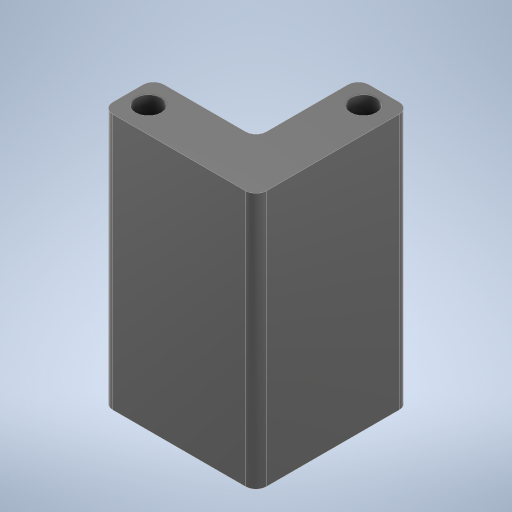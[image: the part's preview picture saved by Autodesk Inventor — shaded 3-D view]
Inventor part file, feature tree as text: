
AUTODESK INVENTOR PART (.ipt)
format: ipt  version: 2024 (Build 280153000, 153)  size: 234,496 bytes
history: native  units: in
note: dims shown in document units (in); Inventor stores cm internally (conversion verified against a paired STEP export)
features: fillet x2, sketch x2, extrude x1, hole x1
ambient origin geometry x8: Origin, YZ Plane, XZ Plane, XY Plane, X Axis, Y Axis, Z Axis, Center Point
bodies: Body1 (feature_tree)
feature tree (6):
  extrude  "Extrusion2"  Depth=1.1811in
  hole  "Hole1"  [1 undecoded]
  fillet  "Fillet1"  Radius=1.9685in
  fillet  "Fillet2"  Radius=0.1575in
  sketch  "Sketch2"  dims[d4=1.1811in d5=1.1811in]
  sketch  "Sketch3"  dims[d6=0.7874in d7=0.7874in d8=1.9685in d9=0.0in d10=0.1969in d11=0.2953in d12=0.1476in d13=0.0984in d14=90.0deg d15=0.3937in d16=0.8108in d17=0.1575in d18=0.1969in d19=0.1575in d20=0.1969in d21=0.0787in d22=0.0787in]
note: 1 required parameter value undecoded (feature->parameter linkage not recoverable at this tier; creation-order binding heuristic only, values carry confidence <= 0.55)
